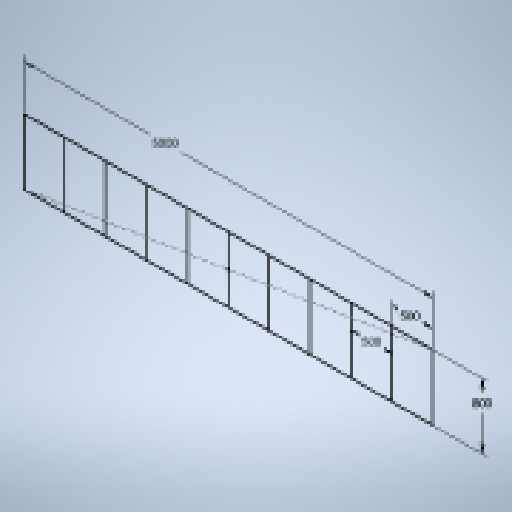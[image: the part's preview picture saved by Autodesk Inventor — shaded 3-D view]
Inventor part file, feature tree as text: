
AUTODESK INVENTOR PART (.ipt)
format: ipt  version: 2025 (Build 290162010, 162A)  size: 137,216 bytes
history: native  units: mm
features: sketch x2
ambient origin geometry x8: Origin, YZ Plane, XZ Plane, XY Plane, X Axis, Y Axis, Z Axis, Center Point
feature tree (2):
  sketch  "Sketch1"  dims[d0=5000.0mm]
  sketch  "Sketch Rectangular Pattern2"  dims[d1=800.0mm d2=500.0mm d10=90.0mm d12=500.0mm d13=10.0mm d15=10.0mm]
